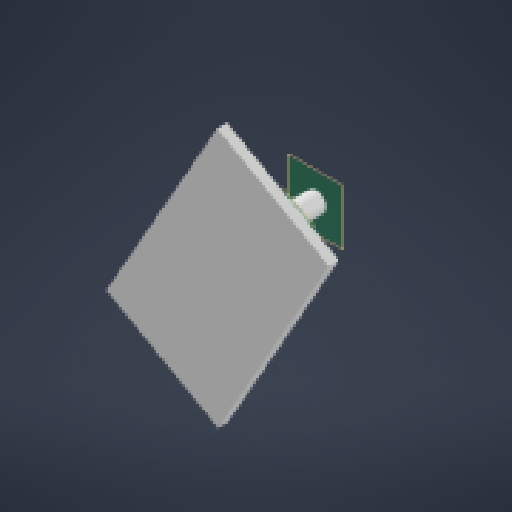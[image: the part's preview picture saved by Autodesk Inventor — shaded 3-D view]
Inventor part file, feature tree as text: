
AUTODESK INVENTOR PART (.ipt)
format: ipt  version: 2024.2 (Build 282272000, 272)  size: 423,424 bytes
history: native  units: in
note: dims shown in document units (in); Inventor stores cm internally (conversion verified against a paired STEP export)
features: extrude x13, sketch x13, fillet x9, plane x8, other x8, reference x4, projected_geometry x4, loft x1
ambient origin geometry x8: Origin, YZ Plane, XZ Plane, XY Plane, X Axis, Y Axis, Z Axis, Center Point
bodies: Solid1 (feature_tree)
feature tree (60):
  extrude  "Extrusion1"  Depth=0.1575in TaperAngle=0.0deg
  plane  "Work Plane1"
  extrude  "Extrusion2"  Depth=2.0in
  extrude  "Extrusion3"  Depth=0.125in
  fillet  "Fillet1"  Radius=0.125in
  fillet  "Fillet2"  Radius=0.8937in
  plane  "Work Plane3"
  plane  "Work Plane5"
  extrude  "Extrusion4"  Depth=0.275in TaperAngle=0.0deg
  extrude  "Extrusion5"  Depth=0.315in TaperAngle=0.0deg
  extrude  "Extrusion6"  Depth=0.315in TaperAngle=0.0deg
  extrude  "Extrusion8"  Depth=0.0787in TaperAngle=0.0deg
  fillet  "Fillet4"  Radius=0.1693in
  plane  "Work Plane2"
  plane  "Work Plane4"
  extrude  "Extrusion7"  Depth=0.2362in
  extrude  "Extrusion9"  Depth=0.0156in
  plane  "Work Plane6"
  extrude  "Extrusion10"  Depth=0.0312in
  loft  "Loft1"
  fillet  "Fillet7"  Radius=0.0787in
  fillet  "Fillet8"  [1 undecoded]
  fillet  "Fillet9"  Radius=0.3228in
  fillet  "Fillet10"  Radius=1.0in
  extrude  "Extrusion11"  Depth=0.3228in
  plane  "Work Plane8"
  sketch  "Sketch12"  dims[d48=0.1693in d49=0.3228in]
  plane  "Work Plane9"
  extrude  "Extrusion12"  Depth=0.0625in
  extrude  "Extrusion13"  Depth=0.0312in
  fillet  "Fillet11"  [1 undecoded]
  fillet  "Fillet12"  [1 undecoded]
  sketch  "Sketch1"  dims[d0=0.1575in d1=0.0in d2=0.1575in d3=0.0in]
  sketch  "Sketch2"  dims[d4=3.5in d5=2.0in]
  sketch  "Sketch3"  dims[d6=0.1575in d7=0.0in d8=0.125in d9=0.125in d10=0.8937in d11=0.0in]
  sketch  "Sketch4"  dims[d13=0.475in d14=0.0in d15=0.275in d16=0.0in]
  reference  "Reference1"
  reference  "Reference2"
  sketch  "Sketch5"  dims[d17=0.1496in d18=0.315in d19=0.0in]
  reference  "Reference3"
  sketch  "Sketch6"  dims[d20=0.1575in d21=0.315in d22=0.0in]
  projected_geometry  "Projected Loop1"
  sketch  "Sketch7"  dims[d23=0.0156in d24=0.0787in d25=0.0in d27=0.1693in]
  projected_geometry  "Projected Loop2"
  sketch  "Sketch8"  dims[d28=0.0787in d29=0.0in d30=0.2362in]
  sketch  "Sketch9"  dims[d32=0.0in d33=90.0deg d34=0.0in d35=90.0deg d36=0.0156in]
  sketch  "Sketch10"  dims[d37=0.0312in d38=0.0312in]
  other  "Edges1"
  other  "Edges2"
  sketch  "Sketch11"  dims[d39=0.0312in d40=0.1693in d41=0.0787in d42=0.0in d44=-0.125in d45=0.3228in d46=1.0in d47=0.0in]
  sketch  "Sketch13"  dims[d50=0.0463in d51=0.0in d52=0.0625in d53=0.0312in]
  reference  "Reference4"
  projected_geometry  "Project Cut Edges1"
  projected_geometry  "Project Cut Edges2"
  other  "<userpath>\Desktop\Robotics\Cad\Powerplay_Fun\Parts\Claw_Assembly.iam"
  other  "Claw_Assembly.iam"
  other  "1611 Series Flanged Ball Bearing (8mm ID x 14mm OD, 5mm Thickness):2"
  other  "1611 Series Flanged Ball Bearing (8mm ID x 14mm OD, 5mm Thickness):3"
  other  "Top_Claw_Mount:1"
  other  "1611 Series Flanged Ball Bearing (8mm ID x 14mm OD, 5mm Thickness):1"
note: 3 required parameter values undecoded (feature->parameter linkage not recoverable at this tier; creation-order binding heuristic only, values carry confidence <= 0.55)
